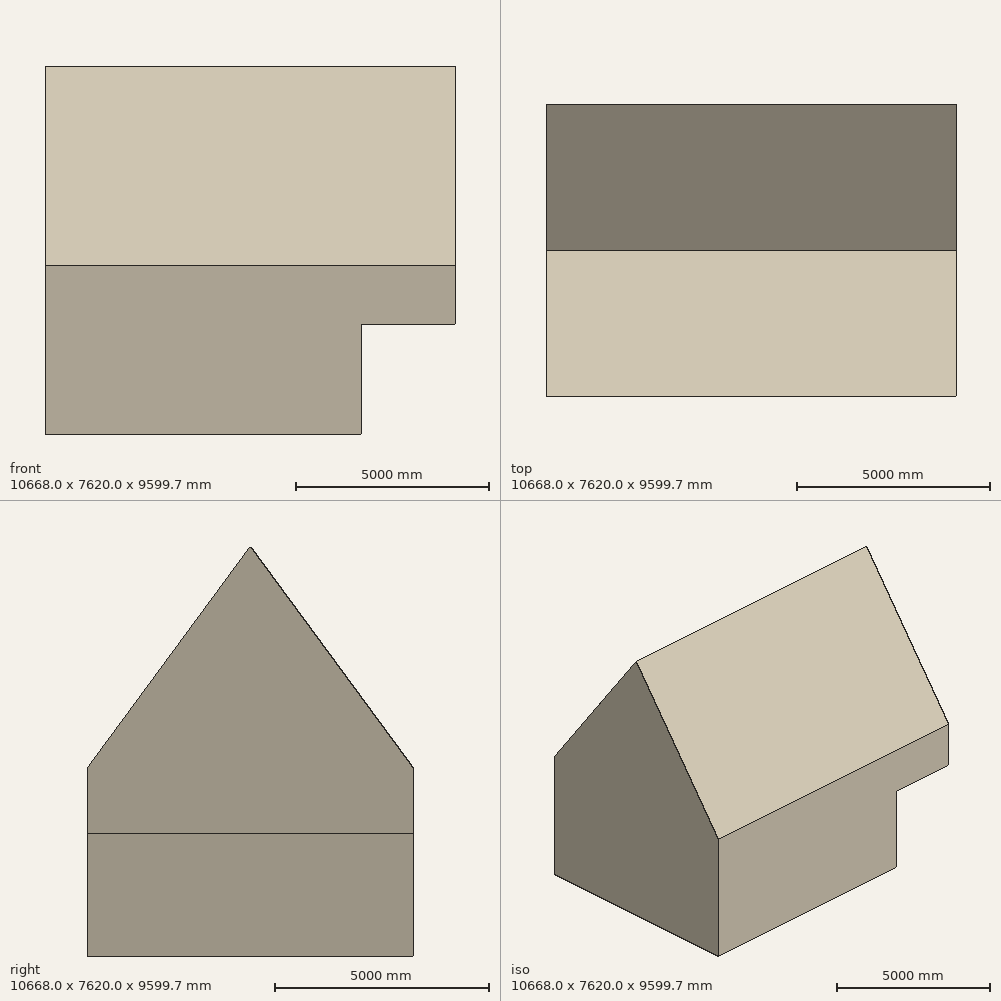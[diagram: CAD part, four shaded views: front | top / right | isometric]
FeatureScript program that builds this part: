
annotation { "Feature Type Name" : "Feature", "Feature Type Description" : "" }
export const myFeature = defineFeature(function(context is Context, id is Id, definition is map)
    precondition{}
    {
        {
            var Q0;
            Q0=qCreatedBy(makeId("Right.planeOp"),FACE);
            var sketch = newSketch(context, id + "F0", { "sketchPlane" : qUnion([Q0])});
            skLineSegment(sketch, "E0.bottom", {"start": v(3810, 2209.8) * mm, "end": v(-3810, 2209.8) * mm});
            skLineSegment(sketch, "E0.top", {"start": v(3810, -2209.8) * mm, "end": v(-3810, -2209.8) * mm});
            skLineSegment(sketch, "E0.left", {"start": v(3810, 2209.8) * mm, "end": v(3810, -2209.8) * mm});
            skLineSegment(sketch, "E0.right", {"start": v(-3810, 2209.8) * mm, "end": v(-3810, -2209.8) * mm});
            skPoint(sketch, "E0.middle", {"position": v(0, 0) * mm});
            skLineSegment(sketch, "E1", {"start": v(3810, 2209.8) * mm, "end": v(0, 7389.9) * mm});
            skLineSegment(sketch, "E2", {"start": v(0, 7389.9) * mm, "end": v(-3810, 2209.8) * mm});
            skSolve(sketch);
        }
        {
            var Q0;
            Q0=makeQuery(id+"F0.imprint","IMPRINT",FACE,{"disambiguationData":[TD([[makeQuery(id+"F0.imprint","IMPRINT",EDGE,{"derivedFrom":sQuery(id+"F0.wireOp",EDGE,"E0.bottom")}),-1.0]])]});
            var Q1;
            Q1=makeQuery(id+"F0.imprint","IMPRINT",FACE,{"disambiguationData":[TD([[makeQuery(id+"F0.imprint","IMPRINT",EDGE,{"derivedFrom":sQuery(id+"F0.wireOp",EDGE,"E0.bottom")}),1.0]])]});
            extrude(context, id + "F1", {"entities" : qUnion([Q0, Q1]), "depth" : 10668 * mm});
        }
        {
            var Q0;
            Q0=makeQuery(id+"F1.opExtrude","CAP_FACE",FACE,{"disambiguationData":[OSD([sQuery(id+"F0.wireOp",EDGE,"E0.top"),sQuery(id+"F0.wireOp",EDGE,"E0.left"),sQuery(id+"F0.wireOp",EDGE,"E0.right"),sQuery(id+"F0.wireOp",EDGE,"E1"),sQuery(id+"F0.wireOp",EDGE,"E2")])],"isStart":false});
            var sketch = newSketch(context, id + "F2", { "sketchPlane" : qUnion([Q0])});
            skLineSegment(sketch, "E3", {"start": v(-3810, 668.8) * mm, "end": v(3810, 668.8) * mm});
            skSolve(sketch);
        }
        {
            var Q0;
            {var subQ0=sQuery(id+"F2.wireOp",EDGE,"E3");Q0=makeQuery(id+"F2.imprint","IMPRINT",FACE,{"disambiguationData":[TD([[makeQuery(id+"F2.imprint","IMPRINT",EDGE,{"derivedFrom":subQ0}),-1.0]])]});}
            extrude(context, id + "F3", {"entities" : qUnion([Q0]), "operationType" : NewBodyOperationType.REMOVE, "oppositeDirection" : true, "depth" : 2438.4 * mm});
        }
    });
